# Revit family: WC-Close Coupled-Stylus Prima II Suite1
name_source: partatom
category: Plumbing Fixtures
revit_build: Autodesk Revit Architecture 2012 (Build: 20110916_2132(x64)
units: mm (PartAtom-declared; Revit-internal decimal feet)

## types (1)
- Standard
    Assembly Code = C1030210
    CW Connection = Yes
    Cost = 318.18 $
    Default Elevation = 0 mm  [stored 0 ft]
    Description = Prima II Vitreous China Close Coupled 4.5/3L Smartflush Suite
    HW Connection = No
    Hardware = Metal-Chrome-Caroma
    Keynote = WC
    Manufacturer = Stylus
    Material_ANZRS = Porcelain-White-Caroma
    Model = PRI400W
    PlumbingMaterial_ANZRS = Porcelain-White-Caroma
    Type Comments = Prima II 4.5/3L Smartflush Close Coupled Toilet Suite
    URL = www.stylus.com.au
    Vent Connection = No
    WELSRating_ANZRS = 4
    Waste Connection = Yes

note: [stored X ft] marks values corroborated as IEEE doubles in the binary element streams (Revit-internal decimal feet)

## geometry (parser evidence)
native form markers: Blend x8, Sweep x2
no freeform markers — native parametric forms only
